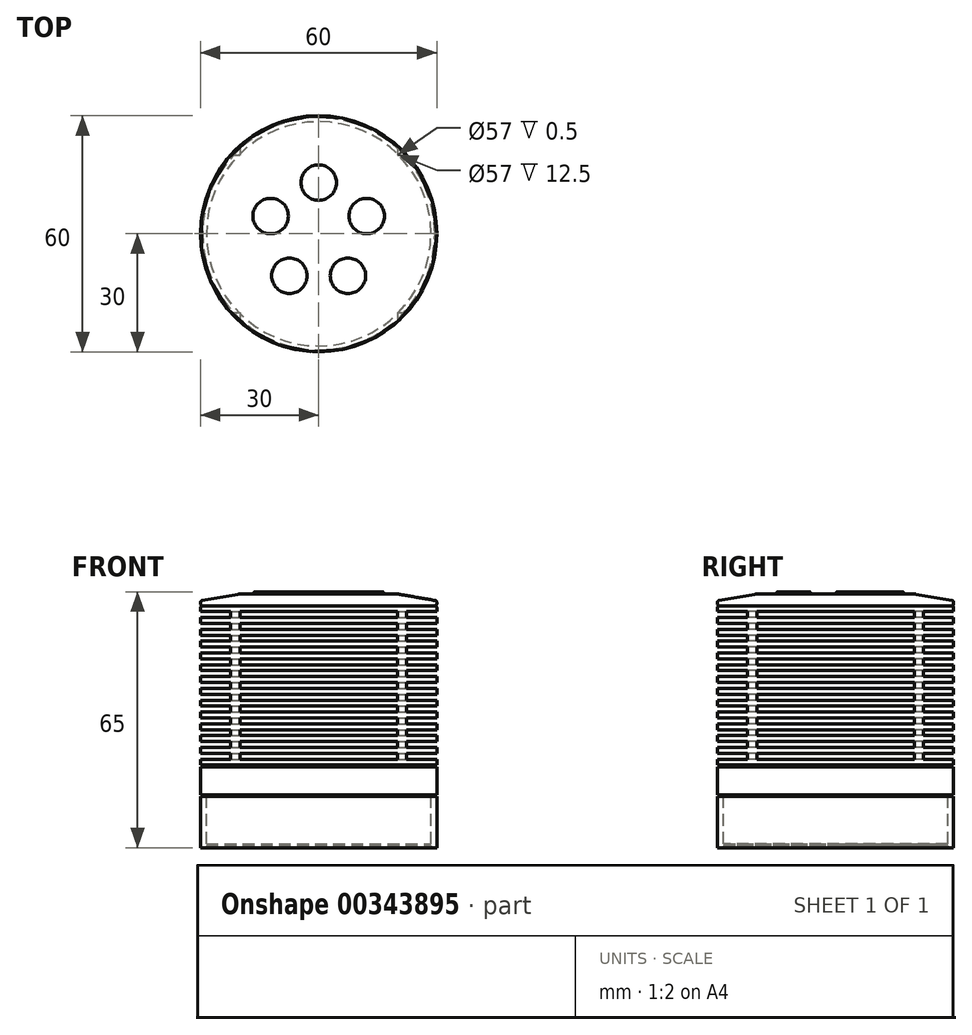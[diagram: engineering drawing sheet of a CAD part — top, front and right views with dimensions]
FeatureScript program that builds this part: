
annotation { "Feature Type Name" : "Feature", "Feature Type Description" : "" }
export const myFeature = defineFeature(function(context is Context, id is Id, definition is map)
    precondition{}
    {
        {
            var Q0;
            Q0=qCreatedBy(makeId("Top.planeOp"),FACE);
            var sketch = newSketch(context, id + "F0", { "sketchPlane" : qUnion([Q0])});
            skCircle(sketch, "E0", {"center": v(0, 0) * mm, "radius": 30 * mm});
            skSolve(sketch);
        }
        {
            var Q0;
            Q0 = qSketchRegion(id + "F0", true);
            extrude(context, id + "F1", {"entities" : qUnion([Q0]), "depth" : 3 * mm});
        }
        {
            var Q0;
            Q0=makeQuery(id+"F1.opExtrude","CAP_EDGE",EDGE,{"disambiguationData":[OSD([sQuery(id+"F0.wireOp",EDGE,"E0")])],"isStart":false});
            chamfer(context, id + "F2", {"entities" : qUnion([Q0]), "chamferType" : ChamferType.OFFSET_ANGLE, "width" : 10 * mm, "oppositeDirection" : false, "angle" : 9.9 * degree, "tangentPropagation" : true});
        }
        {
            var Q0;
            {var subQ0=sQuery(id+"F0.wireOp",EDGE,"E0");Q0=makeQuery(id+"F2.opChamfer","BLEND_EDGE",EDGE,{"blendedFrom":[makeQuery(id+"F1.opExtrude","CAP_EDGE",EDGE,{"disambiguationData":[OSD([subQ0])],"isStart":false}),makeQuery(id+"F1.opExtrude","SWEPT_FACE",FACE,{"disambiguationData":[OSD([subQ0])]})],"blendedInto":[makeQuery(id+"F1.opExtrude","SWEPT_FACE",FACE,{"disambiguationData":[OSD([subQ0])]})]});}
            fillet(context, id + "F3", {"entities" : qUnion([Q0]), "radius" : 0.5 * mm, "tangentPropagation" : true, "rho" : 0.5, "crossSection" : FilletCrossSection.CONIC, "allowEdgeOverflow" : false});
        }
        {
            var Q0;
            {var subQ0=sQuery(id+"F0.wireOp",EDGE,"E0");Q0=makeQuery(id+"F2.opChamfer","BLEND_EDGE",EDGE,{"blendedFrom":[makeQuery(id+"F1.opExtrude","CAP_EDGE",EDGE,{"disambiguationData":[OSD([subQ0])],"isStart":false}),makeQuery(id+"F1.opExtrude","CAP_FACE",FACE,{"disambiguationData":[OSD([subQ0])],"isStart":false})],"blendedInto":[makeQuery(id+"F1.opExtrude","CAP_FACE",FACE,{"disambiguationData":[OSD([subQ0])],"isStart":false})]});}
            fillet(context, id + "F4", {"entities" : qUnion([Q0]), "radius" : 5 * mm, "tangentPropagation" : true, "allowEdgeOverflow" : false});
        }
        {
            var Q0;
            Q0=makeQuery(id+"F1.opExtrude","CAP_FACE",FACE,{"disambiguationData":[OSD([sQuery(id+"F0.wireOp",EDGE,"E0")])],"isStart":false});
            var sketch = newSketch(context, id + "F5", { "sketchPlane" : qUnion([Q0])});
            skCircle(sketch, "E1", {"center": v(0, 13) * mm, "radius": 4.5 * mm});
            skCircle(sketch, "E2", {"center": v(-12.2, 4.5) * mm, "radius": 4.5 * mm});
            skCircle(sketch, "E3", {"center": v(12.2, 4.5) * mm, "radius": 4.5 * mm});
            skCircle(sketch, "E4", {"center": v(-7.43, -10.67) * mm, "radius": 4.5 * mm});
            skCircle(sketch, "E5", {"center": v(7.43, -10.67) * mm, "radius": 4.5 * mm});
            skSolve(sketch);
        }
        {
            var Q0;
            Q0=makeQuery(id+"F5.imprint","IMPRINT",FACE,{"disambiguationData":[TD([[makeQuery(id+"F5.imprint","IMPRINT",EDGE,{"derivedFrom":sQuery(id+"F5.wireOp",EDGE,"E5")}),1.0]])]});
            var Q1;
            Q1=makeQuery(id+"F5.imprint","IMPRINT",FACE,{"disambiguationData":[TD([[makeQuery(id+"F5.imprint","IMPRINT",EDGE,{"derivedFrom":sQuery(id+"F5.wireOp",EDGE,"E4")}),1.0]])]});
            var Q2;
            Q2=makeQuery(id+"F5.imprint","IMPRINT",FACE,{"disambiguationData":[TD([[makeQuery(id+"F5.imprint","IMPRINT",EDGE,{"derivedFrom":sQuery(id+"F5.wireOp",EDGE,"E2")}),1.0]])]});
            var Q3;
            Q3=makeQuery(id+"F5.imprint","IMPRINT",FACE,{"disambiguationData":[TD([[makeQuery(id+"F5.imprint","IMPRINT",EDGE,{"derivedFrom":sQuery(id+"F5.wireOp",EDGE,"E1")}),1.0]])]});
            var Q4;
            Q4=makeQuery(id+"F5.imprint","IMPRINT",FACE,{"disambiguationData":[TD([[makeQuery(id+"F5.imprint","IMPRINT",EDGE,{"derivedFrom":sQuery(id+"F5.wireOp",EDGE,"E3")}),1.0]])]});
            var Q5;
            Q5=sQuery(id+"F5.wireOp",EDGE,"E5");
            var Q6;
            Q6=sQuery(id+"F5.wireOp",EDGE,"E4");
            var Q7;
            Q7=sQuery(id+"F5.wireOp",EDGE,"E2");
            var Q8;
            Q8=sQuery(id+"F5.wireOp",EDGE,"E1");
            var Q9;
            Q9=sQuery(id+"F5.wireOp",EDGE,"E3");
            extrude(context, id + "F6", {"entities" : qUnion([Q0, Q1, Q2, Q3, Q4]), "operationType" : NewBodyOperationType.ADD, "surfaceEntities" : qUnion([Q5, Q6, Q7, Q8, Q9]), "depth" : 0.5 * mm});
        }
        {
            var Q0;
            Q0=makeQuery(id+"F6.opExtrude","CAP_FACE",FACE,{"disambiguationData":[OSD([sQuery(id+"F5.wireOp",EDGE,"E4")])],"isStart":false});
            var Q1;
            Q1=makeQuery(id+"F6.opExtrude","CAP_EDGE",EDGE,{"disambiguationData":[OSD([sQuery(id+"F5.wireOp",EDGE,"E5")])],"isStart":false});
            var Q2;
            Q2=makeQuery(id+"F6.opExtrude","CAP_EDGE",EDGE,{"disambiguationData":[OSD([sQuery(id+"F5.wireOp",EDGE,"E3")])],"isStart":false});
            var Q3;
            Q3=makeQuery(id+"F6.opExtrude","CAP_EDGE",EDGE,{"disambiguationData":[OSD([sQuery(id+"F5.wireOp",EDGE,"E1")])],"isStart":false});
            var Q4;
            Q4=makeQuery(id+"F6.opExtrude","CAP_EDGE",EDGE,{"disambiguationData":[OSD([sQuery(id+"F5.wireOp",EDGE,"E2")])],"isStart":false});
            fillet(context, id + "F7", {"entities" : qUnion([Q0, Q1, Q2, Q3, Q4]), "radius" : 0.5 * mm, "tangentPropagation" : true, "allowEdgeOverflow" : false});
        }
        {
            var Q0;
            Q0=makeQuery(id+"F1.opExtrude","CAP_FACE",FACE,{"disambiguationData":[OSD([sQuery(id+"F0.wireOp",EDGE,"E0")])],"isStart":true});
            var sketch = newSketch(context, id + "F8", { "sketchPlane" : qUnion([Q0])});
            skSolve(sketch);
        }
        {
            var Q0;
            Q0=makeQuery(id+"F1.opExtrude","CAP_EDGE",EDGE,{"disambiguationData":[OSD([sQuery(id+"F0.wireOp",EDGE,"E0")])],"isStart":true});
            fillet(context, id + "F9", {"entities" : qUnion([Q0]), "radius" : 0.5 * mm, "tangentPropagation" : true, "allowEdgeOverflow" : false});
        }
        {
            var Q0;
            Q0=makeQuery(id+"F8.imprint","IMPRINT",FACE,{"disambiguationData":[TD([[makeQuery(id+"F8.imprint","IMPRINT",EDGE,{"derivedFrom":makeQuery(id+"F1.opExtrude","CAP_EDGE",EDGE,{"disambiguationData":[OSD([sQuery(id+"F0.wireOp",EDGE,"E0")])],"isStart":true})}),-1.0]])]});
            var sketch = newSketch(context, id + "F10", { "sketchPlane" : qUnion([Q0])});
            skSolve(sketch);
        }
        {
            var Q0;
            Q0 = qSketchRegion(id + "F10", true);
            var Q1;
            Q1=makeQuery(id+"F8.imprint","IMPRINT",FACE,{"disambiguationData":[TD([[makeQuery(id+"F8.imprint","IMPRINT",EDGE,{"derivedFrom":makeQuery(id+"F1.opExtrude","CAP_EDGE",EDGE,{"disambiguationData":[OSD([sQuery(id+"F0.wireOp",EDGE,"E0")])],"isStart":true})}),-1.0]])]});
            extrude(context, id + "F11", {"entities" : qUnion([Q0, Q1]), "operationType" : NewBodyOperationType.ADD, "depth" : 40.5 * mm});
        }
        {
            var Q0;
            Q0=makeQuery(id+"F11.opExtrude","CAP_EDGE",EDGE,{"disambiguationData":[OSD([sQuery(id+"F0.wireOp",EDGE,"E0")])],"isStart":true});
            fillet(context, id + "F12", {"entities" : qUnion([Q0]), "radius" : 0.5 * mm, "allowEdgeOverflow" : false});
        }
        {
            var Q0;
            Q0=qCreatedBy(makeId("Front.planeOp"),FACE);
            var sketch = newSketch(context, id + "F13", { "sketchPlane" : qUnion([Q0])});
            skLineSegment(sketch, "E6", {"start": v(0, 0) * mm, "end": v(0, -1.5) * mm});
            skLineSegment(sketch, "E7", {"start": v(0, -15) * mm, "end": v(0, -16.5) * mm});
            skLineSegment(sketch, "E8", {"start": v(0, -18) * mm, "end": v(0, -19.5) * mm});
            skLineSegment(sketch, "E9", {"start": v(0, -21) * mm, "end": v(0, -22.5) * mm});
            skLineSegment(sketch, "E10", {"start": v(0, -24) * mm, "end": v(0, -25.5) * mm});
            skLineSegment(sketch, "E11", {"start": v(0, -27) * mm, "end": v(0, -28.5) * mm});
            skLineSegment(sketch, "E12", {"start": v(0, -30) * mm, "end": v(0, -31.5) * mm});
            skLineSegment(sketch, "E13", {"start": v(0, -33) * mm, "end": v(0, -34.5) * mm});
            skLineSegment(sketch, "E14", {"start": v(0, -36) * mm, "end": v(0, -37.5) * mm});
            skLineSegment(sketch, "E15", {"start": v(0, -39) * mm, "end": v(0, -40.5) * mm});
            skLineSegment(sketch, "E16", {"start": v(0, -1.5) * mm, "end": v(0, -3) * mm});
            skLineSegment(sketch, "E17", {"start": v(0, -3) * mm, "end": v(0, -4.5) * mm});
            skLineSegment(sketch, "E18", {"start": v(0, -6) * mm, "end": v(0, -7.5) * mm});
            skLineSegment(sketch, "E19", {"start": v(0, -9) * mm, "end": v(0, -10.5) * mm});
            skLineSegment(sketch, "E20", {"start": v(0, -12) * mm, "end": v(0, -13.5) * mm});
            skLineSegment(sketch, "E21", {"start": v(0, -13.5) * mm, "end": v(0, -15) * mm});
            skLineSegment(sketch, "E22.top", {"start": v(0, -1.5) * mm, "end": v(-20, -1.5) * mm});
            skLineSegment(sketch, "E23.bottom", {"start": v(-20, -1.5) * mm, "end": v(20, -1.5) * mm});
            skLineSegment(sketch, "E23.top", {"start": v(-20, -3) * mm, "end": v(20, -3) * mm});
            skLineSegment(sketch, "E23.left", {"start": v(-20, -1.5) * mm, "end": v(-20, -3) * mm});
            skLineSegment(sketch, "E23.right", {"start": v(20, -1.5) * mm, "end": v(20, -3) * mm});
            skLineSegment(sketch, "E24.bottom", {"start": v(0, -13.5) * mm, "end": v(-20, -13.5) * mm});
            skLineSegment(sketch, "E24.top", {"start": v(0, -15) * mm, "end": v(-20, -15) * mm});
            skLineSegment(sketch, "E24.right", {"start": v(-20, -13.5) * mm, "end": v(-20, -15) * mm});
            skLineSegment(sketch, "E25.bottom", {"start": v(-20, -13.5) * mm, "end": v(20, -13.5) * mm});
            skLineSegment(sketch, "E25.top", {"start": v(-20, -15) * mm, "end": v(20, -15) * mm});
            skLineSegment(sketch, "E25.right", {"start": v(20, -13.5) * mm, "end": v(20, -15) * mm});
            skLineSegment(sketch, "E26.bottom", {"start": v(-20, -16.5) * mm, "end": v(20, -16.5) * mm});
            skLineSegment(sketch, "E26.top", {"start": v(-20, -18) * mm, "end": v(20, -18) * mm});
            skLineSegment(sketch, "E26.left", {"start": v(-20, -16.5) * mm, "end": v(-20, -18) * mm});
            skLineSegment(sketch, "E26.right", {"start": v(20, -16.5) * mm, "end": v(20, -18) * mm});
            skLineSegment(sketch, "E27.bottom", {"start": v(-20, -19.5) * mm, "end": v(20, -19.5) * mm});
            skLineSegment(sketch, "E27.top", {"start": v(-20, -21) * mm, "end": v(20, -21) * mm});
            skLineSegment(sketch, "E27.left", {"start": v(-20, -19.5) * mm, "end": v(-20, -21) * mm});
            skLineSegment(sketch, "E27.right", {"start": v(20, -19.5) * mm, "end": v(20, -21) * mm});
            skLineSegment(sketch, "E28.bottom", {"start": v(-20, -22.5) * mm, "end": v(20, -22.5) * mm});
            skLineSegment(sketch, "E28.top", {"start": v(-20, -24) * mm, "end": v(20, -24) * mm});
            skLineSegment(sketch, "E28.left", {"start": v(-20, -22.5) * mm, "end": v(-20, -24) * mm});
            skLineSegment(sketch, "E28.right", {"start": v(20, -22.5) * mm, "end": v(20, -24) * mm});
            skLineSegment(sketch, "E29.bottom", {"start": v(-20, -25.5) * mm, "end": v(20, -25.5) * mm});
            skLineSegment(sketch, "E29.top", {"start": v(-20, -27) * mm, "end": v(20, -27) * mm});
            skLineSegment(sketch, "E29.left", {"start": v(-20, -25.5) * mm, "end": v(-20, -27) * mm});
            skLineSegment(sketch, "E29.right", {"start": v(20, -25.5) * mm, "end": v(20, -27) * mm});
            skLineSegment(sketch, "E30.bottom", {"start": v(-20, -28.5) * mm, "end": v(20, -28.5) * mm});
            skLineSegment(sketch, "E30.top", {"start": v(-20, -30) * mm, "end": v(20, -30) * mm});
            skLineSegment(sketch, "E30.left", {"start": v(-20, -28.5) * mm, "end": v(-20, -30) * mm});
            skLineSegment(sketch, "E30.right", {"start": v(20, -28.5) * mm, "end": v(20, -30) * mm});
            skLineSegment(sketch, "E31.bottom", {"start": v(-20, -31.5) * mm, "end": v(20, -31.5) * mm});
            skLineSegment(sketch, "E31.top", {"start": v(-20, -33) * mm, "end": v(20, -33) * mm});
            skLineSegment(sketch, "E31.left", {"start": v(-20, -31.5) * mm, "end": v(-20, -33) * mm});
            skLineSegment(sketch, "E31.right", {"start": v(20, -31.5) * mm, "end": v(20, -33) * mm});
            skLineSegment(sketch, "E32.bottom", {"start": v(-20, -34.5) * mm, "end": v(20, -34.5) * mm});
            skLineSegment(sketch, "E32.top", {"start": v(-20, -36) * mm, "end": v(20, -36) * mm});
            skLineSegment(sketch, "E32.left", {"start": v(-20, -34.5) * mm, "end": v(-20, -36) * mm});
            skLineSegment(sketch, "E32.right", {"start": v(20, -34.5) * mm, "end": v(20, -36) * mm});
            skLineSegment(sketch, "E33.bottom", {"start": v(-20, -37.5) * mm, "end": v(20, -37.5) * mm});
            skLineSegment(sketch, "E33.top", {"start": v(-20, -39) * mm, "end": v(20, -39) * mm});
            skLineSegment(sketch, "E33.left", {"start": v(-20, -37.5) * mm, "end": v(-20, -39) * mm});
            skLineSegment(sketch, "E33.right", {"start": v(20, -37.5) * mm, "end": v(20, -39) * mm});
            skLineSegment(sketch, "E34.bottom", {"start": v(-20, -4.5) * mm, "end": v(20, -4.5) * mm});
            skLineSegment(sketch, "E34.top", {"start": v(-20, -6) * mm, "end": v(20, -6) * mm});
            skLineSegment(sketch, "E34.left", {"start": v(-20, -4.5) * mm, "end": v(-20, -6) * mm});
            skLineSegment(sketch, "E34.right", {"start": v(20, -4.5) * mm, "end": v(20, -6) * mm});
            skLineSegment(sketch, "E35.bottom", {"start": v(-20, -7.5) * mm, "end": v(20, -7.5) * mm});
            skLineSegment(sketch, "E35.top", {"start": v(-20, -9) * mm, "end": v(20, -9) * mm});
            skLineSegment(sketch, "E35.left", {"start": v(-20, -7.5) * mm, "end": v(-20, -9) * mm});
            skLineSegment(sketch, "E35.right", {"start": v(20, -7.5) * mm, "end": v(20, -9) * mm});
            skLineSegment(sketch, "E36.bottom", {"start": v(-20, -10.5) * mm, "end": v(20, -10.5) * mm});
            skLineSegment(sketch, "E36.top", {"start": v(-20, -12) * mm, "end": v(20, -12) * mm});
            skLineSegment(sketch, "E36.left", {"start": v(-20, -10.5) * mm, "end": v(-20, -12) * mm});
            skLineSegment(sketch, "E36.right", {"start": v(20, -10.5) * mm, "end": v(20, -12) * mm});
            skSolve(sketch);
        }
        {
            var Q0;
            Q0 = qSketchRegion(id + "F13", true);
            extrude(context, id + "F14", {"entities" : qUnion([Q0]), "operationType" : NewBodyOperationType.REMOVE, "endBound" : BoundingType.SYMMETRIC, "oppositeDirection" : true, "depth" : 60 * mm});
        }
        {
            var Q0;
            Q0=qCreatedBy(makeId("Right.planeOp"),FACE);
            var sketch = newSketch(context, id + "F15", { "sketchPlane" : qUnion([Q0])});
            skLineSegment(sketch, "E37.top", {"start": v(0, -1.5) * mm, "end": v(-20, -1.5) * mm});
            skLineSegment(sketch, "E38.bottom", {"start": v(-20, -1.5) * mm, "end": v(20, -1.5) * mm});
            skLineSegment(sketch, "E38.top", {"start": v(-20, -3) * mm, "end": v(20, -3) * mm});
            skLineSegment(sketch, "E38.left", {"start": v(-20, -1.5) * mm, "end": v(-20, -3) * mm});
            skLineSegment(sketch, "E38.right", {"start": v(20, -1.5) * mm, "end": v(20, -3) * mm});
            skLineSegment(sketch, "E39", {"start": v(0, -3) * mm, "end": v(0, -4.5) * mm});
            skPoint(sketch, "E39.endSnap0", {"position": v(0, -3) * mm});
            skLineSegment(sketch, "E40", {"start": v(0, -4.5) * mm, "end": v(0, -6) * mm});
            skLineSegment(sketch, "E41", {"start": v(0, -6) * mm, "end": v(0, -7.5) * mm});
            skLineSegment(sketch, "E42", {"start": v(0, -7.5) * mm, "end": v(0, -9) * mm});
            skLineSegment(sketch, "E43", {"start": v(0, -9) * mm, "end": v(0, -10.5) * mm});
            skLineSegment(sketch, "E44", {"start": v(0, -10.5) * mm, "end": v(0, -12) * mm});
            skLineSegment(sketch, "E45", {"start": v(0, -12) * mm, "end": v(0, -13.5) * mm});
            skLineSegment(sketch, "E46", {"start": v(0, -13.5) * mm, "end": v(0, -15) * mm});
            skLineSegment(sketch, "E47", {"start": v(0, -15) * mm, "end": v(0, -16.5) * mm});
            skLineSegment(sketch, "E48", {"start": v(0, -16.5) * mm, "end": v(0, -18) * mm});
            skLineSegment(sketch, "E49", {"start": v(0, -18) * mm, "end": v(0, -19.5) * mm});
            skLineSegment(sketch, "E50", {"start": v(0, -19.5) * mm, "end": v(0, -21) * mm});
            skLineSegment(sketch, "E51", {"start": v(0, -21) * mm, "end": v(0, -22.5) * mm});
            skLineSegment(sketch, "E52", {"start": v(0, -22.5) * mm, "end": v(0, -24) * mm});
            skLineSegment(sketch, "E53", {"start": v(0, -24) * mm, "end": v(0, -25.5) * mm});
            skLineSegment(sketch, "E54", {"start": v(0, -25.5) * mm, "end": v(0, -27) * mm});
            skLineSegment(sketch, "E55", {"start": v(0, -27) * mm, "end": v(0, -28.5) * mm});
            skLineSegment(sketch, "E56", {"start": v(0, -28.5) * mm, "end": v(0, -30) * mm});
            skLineSegment(sketch, "E57", {"start": v(0, -30) * mm, "end": v(0, -31.5) * mm});
            skLineSegment(sketch, "E58", {"start": v(0, -31.5) * mm, "end": v(0, -33) * mm});
            skLineSegment(sketch, "E59", {"start": v(0, -33) * mm, "end": v(0, -34.5) * mm});
            skLineSegment(sketch, "E60", {"start": v(0, -34.5) * mm, "end": v(0, -36) * mm});
            skLineSegment(sketch, "E61", {"start": v(0, -36) * mm, "end": v(0, -37.5) * mm});
            skLineSegment(sketch, "E62", {"start": v(0, -37.5) * mm, "end": v(0, -39) * mm});
            skLineSegment(sketch, "E63", {"start": v(0, -39) * mm, "end": v(0, -40.5) * mm});
            skLineSegment(sketch, "E64.bottom", {"start": v(-20, -4.5) * mm, "end": v(20, -4.5) * mm});
            skLineSegment(sketch, "E64.top", {"start": v(-20, -6) * mm, "end": v(20, -6) * mm});
            skLineSegment(sketch, "E64.left", {"start": v(-20, -4.5) * mm, "end": v(-20, -6) * mm});
            skLineSegment(sketch, "E64.right", {"start": v(20, -4.5) * mm, "end": v(20, -6) * mm});
            skLineSegment(sketch, "E65.bottom", {"start": v(-20, -7.5) * mm, "end": v(20, -7.5) * mm});
            skLineSegment(sketch, "E65.top", {"start": v(-20, -9) * mm, "end": v(20, -9) * mm});
            skLineSegment(sketch, "E65.left", {"start": v(-20, -7.5) * mm, "end": v(-20, -9) * mm});
            skLineSegment(sketch, "E65.right", {"start": v(20, -7.5) * mm, "end": v(20, -9) * mm});
            skLineSegment(sketch, "E66.bottom", {"start": v(-20, -10.5) * mm, "end": v(20, -10.5) * mm});
            skLineSegment(sketch, "E66.top", {"start": v(-20, -12) * mm, "end": v(20, -12) * mm});
            skLineSegment(sketch, "E66.left", {"start": v(-20, -10.5) * mm, "end": v(-20, -12) * mm});
            skLineSegment(sketch, "E66.right", {"start": v(20, -10.5) * mm, "end": v(20, -12) * mm});
            skLineSegment(sketch, "E67.bottom", {"start": v(-20, -13.5) * mm, "end": v(20, -13.5) * mm});
            skLineSegment(sketch, "E67.top", {"start": v(-20, -15) * mm, "end": v(20, -15) * mm});
            skLineSegment(sketch, "E67.left", {"start": v(-20, -13.5) * mm, "end": v(-20, -15) * mm});
            skLineSegment(sketch, "E67.right", {"start": v(20, -13.5) * mm, "end": v(20, -15) * mm});
            skLineSegment(sketch, "E68.bottom", {"start": v(-20, -16.5) * mm, "end": v(20, -16.5) * mm});
            skLineSegment(sketch, "E68.top", {"start": v(-20, -18) * mm, "end": v(20, -18) * mm});
            skLineSegment(sketch, "E68.left", {"start": v(-20, -16.5) * mm, "end": v(-20, -18) * mm});
            skLineSegment(sketch, "E68.right", {"start": v(20, -16.5) * mm, "end": v(20, -18) * mm});
            skLineSegment(sketch, "E69.bottom", {"start": v(-20, -19.5) * mm, "end": v(20, -19.5) * mm});
            skLineSegment(sketch, "E69.top", {"start": v(-20, -21) * mm, "end": v(20, -21) * mm});
            skLineSegment(sketch, "E69.left", {"start": v(-20, -19.5) * mm, "end": v(-20, -21) * mm});
            skLineSegment(sketch, "E69.right", {"start": v(20, -19.5) * mm, "end": v(20, -21) * mm});
            skLineSegment(sketch, "E70.bottom", {"start": v(-20, -22.5) * mm, "end": v(20, -22.5) * mm});
            skLineSegment(sketch, "E70.top", {"start": v(-20, -24) * mm, "end": v(20, -24) * mm});
            skLineSegment(sketch, "E70.left", {"start": v(-20, -22.5) * mm, "end": v(-20, -24) * mm});
            skLineSegment(sketch, "E70.right", {"start": v(20, -22.5) * mm, "end": v(20, -24) * mm});
            skLineSegment(sketch, "E71.bottom", {"start": v(-20, -25.5) * mm, "end": v(20, -25.5) * mm});
            skLineSegment(sketch, "E71.top", {"start": v(-20, -27) * mm, "end": v(20, -27) * mm});
            skLineSegment(sketch, "E71.left", {"start": v(-20, -25.5) * mm, "end": v(-20, -27) * mm});
            skLineSegment(sketch, "E71.right", {"start": v(20, -25.5) * mm, "end": v(20, -27) * mm});
            skLineSegment(sketch, "E72.bottom", {"start": v(-20, -28.5) * mm, "end": v(20, -28.5) * mm});
            skLineSegment(sketch, "E72.top", {"start": v(-20, -30) * mm, "end": v(20, -30) * mm});
            skLineSegment(sketch, "E72.left", {"start": v(-20, -28.5) * mm, "end": v(-20, -30) * mm});
            skLineSegment(sketch, "E72.right", {"start": v(20, -28.5) * mm, "end": v(20, -30) * mm});
            skLineSegment(sketch, "E73.bottom", {"start": v(-20, -31.5) * mm, "end": v(20, -31.5) * mm});
            skLineSegment(sketch, "E73.top", {"start": v(-20, -33) * mm, "end": v(20, -33) * mm});
            skLineSegment(sketch, "E73.left", {"start": v(-20, -31.5) * mm, "end": v(-20, -33) * mm});
            skLineSegment(sketch, "E73.right", {"start": v(20, -31.5) * mm, "end": v(20, -33) * mm});
            skLineSegment(sketch, "E74.bottom", {"start": v(-20, -34.5) * mm, "end": v(20, -34.5) * mm});
            skLineSegment(sketch, "E74.top", {"start": v(-20, -36) * mm, "end": v(20, -36) * mm});
            skLineSegment(sketch, "E74.left", {"start": v(-20, -34.5) * mm, "end": v(-20, -36) * mm});
            skLineSegment(sketch, "E74.right", {"start": v(20, -34.5) * mm, "end": v(20, -36) * mm});
            skLineSegment(sketch, "E75.bottom", {"start": v(-20, -37.5) * mm, "end": v(20, -37.5) * mm});
            skLineSegment(sketch, "E75.top", {"start": v(-20, -39) * mm, "end": v(20, -39) * mm});
            skLineSegment(sketch, "E75.left", {"start": v(-20, -37.5) * mm, "end": v(-20, -39) * mm});
            skLineSegment(sketch, "E75.right", {"start": v(20, -37.5) * mm, "end": v(20, -39) * mm});
            skSolve(sketch);
        }
        {
            var Q0;
            Q0 = qSketchRegion(id + "F15", true);
            extrude(context, id + "F16", {"entities" : qUnion([Q0]), "operationType" : NewBodyOperationType.REMOVE, "endBound" : BoundingType.SYMMETRIC, "oppositeDirection" : true, "depth" : 60 * mm});
        }
        {
            var Q0;
            Q0=makeQuery(id+"F11.opExtrude","CAP_FACE",FACE,{"disambiguationData":[OSD([sQuery(id+"F0.wireOp",EDGE,"E0")])],"isStart":false});
            var sketch = newSketch(context, id + "F17", { "sketchPlane" : qUnion([Q0])});
            skCircle(sketch, "E76", {"center": v(0, 0) * mm, "radius": 29.5 * mm});
            skSolve(sketch);
        }
        {
            var Q0;
            Q0 = qSketchRegion(id + "F17", true);
            extrude(context, id + "F18", {"entities" : qUnion([Q0]), "operationType" : NewBodyOperationType.ADD, "depth" : 0.5 * mm});
        }
        {
            var Q0;
            Q0=makeQuery(id+"F18.opExtrude","CAP_FACE",FACE,{"disambiguationData":[OSD([sQuery(id+"F17.wireOp",EDGE,"E76")])],"isStart":false});
            var sketch = newSketch(context, id + "F19", { "sketchPlane" : qUnion([Q0])});
            skCircle(sketch, "E77", {"center": v(0, 0) * mm, "radius": 30 * mm});
            skSolve(sketch);
        }
        {
            var Q0;
            Q0 = qSketchRegion(id + "F19", true);
            extrude(context, id + "F20", {"entities" : qUnion([Q0]), "operationType" : NewBodyOperationType.ADD, "depth" : 7 * mm});
        }
        {
            var Q0;
            Q0=makeQuery(id+"F20.opExtrude","CAP_FACE",FACE,{"disambiguationData":[OSD([sQuery(id+"F19.wireOp",EDGE,"E77")])],"isStart":false});
            var sketch = newSketch(context, id + "F21", { "sketchPlane" : qUnion([Q0])});
            skCircle(sketch, "E78", {"center": v(0, 0) * mm, "radius": 29.5 * mm});
            skSolve(sketch);
        }
        {
            var Q0;
            Q0 = qSketchRegion(id + "F21", true);
            extrude(context, id + "F22", {"entities" : qUnion([Q0]), "operationType" : NewBodyOperationType.ADD, "depth" : 0.5 * mm});
        }
        {
            var Q0;
            Q0=makeQuery(id+"F22.opExtrude","CAP_FACE",FACE,{"disambiguationData":[OSD([sQuery(id+"F21.wireOp",EDGE,"E78")])],"isStart":false});
            var sketch = newSketch(context, id + "F23", { "sketchPlane" : qUnion([Q0])});
            skCircle(sketch, "E79", {"center": v(0, 0) * mm, "radius": 30 * mm});
            skSolve(sketch);
        }
        {
            var Q0;
            Q0 = qSketchRegion(id + "F23", true);
            extrude(context, id + "F24", {"entities" : qUnion([Q0]), "operationType" : NewBodyOperationType.ADD, "depth" : 13 * mm});
        }
        {
            var Q0;
            Q0=makeQuery(id+"F20.opExtrude","CAP_FACE",FACE,{"disambiguationData":[OSD([sQuery(id+"F19.wireOp",EDGE,"E77")])],"isStart":false});
            var sketch = newSketch(context, id + "F25", { "sketchPlane" : qUnion([Q0])});
            skCircle(sketch, "E80", {"center": v(0, 0) * mm, "radius": 28.5 * mm});
            skSolve(sketch);
        }
        {
            var Q0;
            Q0 = qSketchRegion(id + "F25", true);
            extrude(context, id + "F26", {"entities" : qUnion([Q0]), "operationType" : NewBodyOperationType.REMOVE, "depth" : 12.5 * mm});
        }
        {
            var Q0;
            Q0=makeQuery(id+"F24.opExtrude","CAP_FACE",FACE,{"disambiguationData":[OSD([sQuery(id+"F23.wireOp",EDGE,"E79")])],"isStart":false});
            var sketch = newSketch(context, id + "F27", { "sketchPlane" : qUnion([Q0])});
            skCircle(sketch, "E81", {"center": v(0, 0) * mm, "radius": 28.5 * mm});
            skSolve(sketch);
        }
        {
            var Q0;
            Q0 = qSketchRegion(id + "F27", true);
            extrude(context, id + "F28", {"entities" : qUnion([Q0]), "operationType" : NewBodyOperationType.REMOVE, "oppositeDirection" : true, "depth" : 0.5 * mm});
        }
    });
